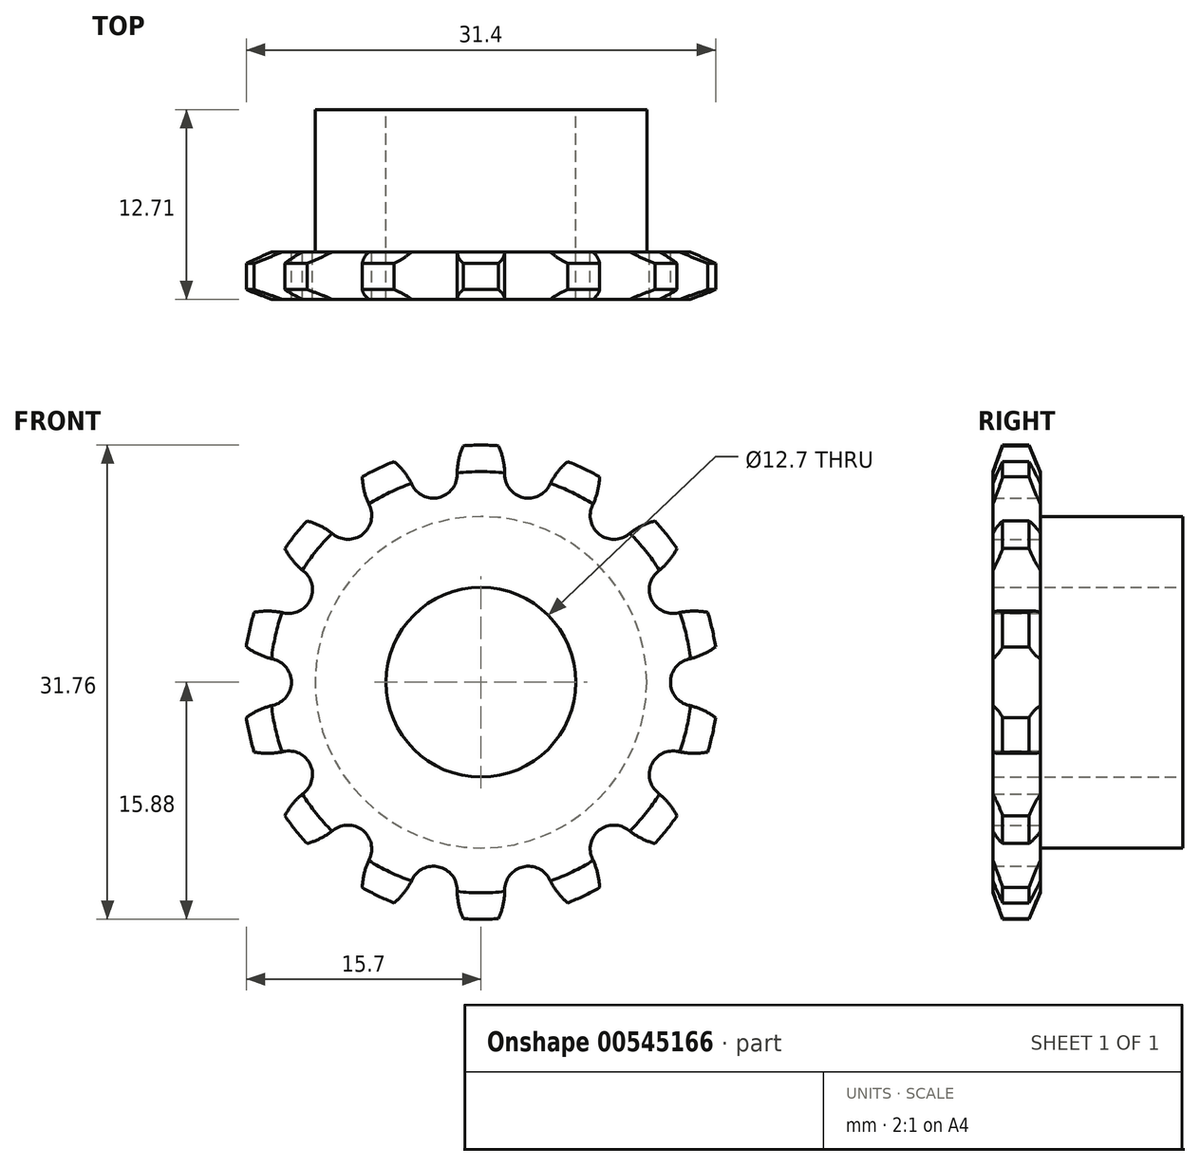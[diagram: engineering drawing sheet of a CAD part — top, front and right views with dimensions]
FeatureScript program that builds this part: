
annotation { "Feature Type Name" : "Feature", "Feature Type Description" : "" }
export const myFeature = defineFeature(function(context is Context, id is Id, definition is map)
    precondition{}
    {
        {
            var Q0;
            Q0=qCreatedBy(makeId("Front.planeOp"),FACE);
            var sketch = newSketch(context, id + "F0", { "sketchPlane" : qUnion([Q0])});
            skCircle(sketch, "E0.cCircle", {"center": v(0, 0) * mm, "radius": 13.91 * mm, "construction": true});
            skLineSegment(sketch, "E0.0", {"start": v(-3.17, 13.91) * mm, "end": v(3.17, 13.91) * mm, "construction": true});
            skLineSegment(sketch, "E0.1", {"start": v(3.18, 13.91) * mm, "end": v(8.9, 11.16) * mm, "construction": true});
            skLineSegment(sketch, "E0.2", {"start": v(8.9, 11.16) * mm, "end": v(12.86, 6.2) * mm, "construction": true});
            skLineSegment(sketch, "E0.3", {"start": v(12.86, 6.2) * mm, "end": v(14.27, 0) * mm, "construction": true});
            skLineSegment(sketch, "E0.4", {"start": v(14.27, 0) * mm, "end": v(12.86, -6.2) * mm, "construction": true});
            skLineSegment(sketch, "E0.5", {"start": v(12.86, -6.2) * mm, "end": v(8.9, -11.16) * mm, "construction": true});
            skLineSegment(sketch, "E0.6", {"start": v(8.9, -11.16) * mm, "end": v(3.18, -13.91) * mm, "construction": true});
            skLineSegment(sketch, "E0.7", {"start": v(3.17, -13.91) * mm, "end": v(-3.17, -13.91) * mm, "construction": true});
            skLineSegment(sketch, "E0.8", {"start": v(-3.17, -13.91) * mm, "end": v(-8.9, -11.16) * mm, "construction": true});
            skLineSegment(sketch, "E0.9", {"start": v(-8.9, -11.16) * mm, "end": v(-12.86, -6.2) * mm, "construction": true});
            skLineSegment(sketch, "E0.10", {"start": v(-12.86, -6.2) * mm, "end": v(-14.27, 0) * mm, "construction": true});
            skLineSegment(sketch, "E0.11", {"start": v(-14.27, 0) * mm, "end": v(-12.86, 6.2) * mm, "construction": true});
            skLineSegment(sketch, "E0.12", {"start": v(-12.86, 6.2) * mm, "end": v(-8.9, 11.16) * mm, "construction": true});
            skLineSegment(sketch, "E0.13", {"start": v(-8.9, 11.16) * mm, "end": v(-3.18, 13.91) * mm, "construction": true});
            skPoint(sketch, "E0.0.midPoint", {"position": v(0, 13.91) * mm});
            skCircle(sketch, "E1", {"center": v(3.17, 13.91) * mm, "radius": 1.59 * mm});
            skCircle(sketch, "E2", {"center": v(-3.17, 13.91) * mm, "radius": 1.59 * mm});
            skCircle(sketch, "E3", {"center": v(8.9, 11.16) * mm, "radius": 1.59 * mm});
            skCircle(sketch, "E4", {"center": v(-8.9, 11.16) * mm, "radius": 1.59 * mm});
            skCircle(sketch, "E5", {"center": v(-12.86, 6.2) * mm, "radius": 1.59 * mm});
            skCircle(sketch, "E6", {"center": v(-14.27, 0) * mm, "radius": 1.59 * mm});
            skCircle(sketch, "E7", {"center": v(12.86, 6.2) * mm, "radius": 1.59 * mm});
            skCircle(sketch, "E8", {"center": v(14.27, 0) * mm, "radius": 1.59 * mm});
            skCircle(sketch, "E9", {"center": v(12.86, -6.2) * mm, "radius": 1.59 * mm});
            skCircle(sketch, "E10", {"center": v(8.9, -11.16) * mm, "radius": 1.59 * mm});
            skCircle(sketch, "E11", {"center": v(3.18, -13.91) * mm, "radius": 1.59 * mm});
            skCircle(sketch, "E12", {"center": v(-12.86, -6.2) * mm, "radius": 1.59 * mm});
            skCircle(sketch, "E13", {"center": v(-8.9, -11.16) * mm, "radius": 1.59 * mm});
            skCircle(sketch, "E14", {"center": v(-3.17, -13.91) * mm, "radius": 1.59 * mm});
            skCircle(sketch, "E15", {"center": v(0, 0) * mm, "radius": 15.88 * mm});
            skArc(sketch, "E16", {"start": v(-1.59, 13.91) * mm, "mid": v(-1.17, 15.85) * mm, "end": v(0, 17.46) * mm});
            skArc(sketch, "E17", {"start": v(1.59, 13.91) * mm, "mid": v(1.17, 15.85) * mm, "end": v(0, 17.46) * mm});
            skArc(sketch, "E18", {"start": v(7.47, 11.84) * mm, "mid": v(7.94, 13.78) * mm, "end": v(7.58, 15.73) * mm});
            skArc(sketch, "E19", {"start": v(4.6, 13.22) * mm, "mid": v(5.82, 14.8) * mm, "end": v(7.58, 15.73) * mm});
            skArc(sketch, "E20", {"start": v(11.87, 7.43) * mm, "mid": v(13.13, 8.97) * mm, "end": v(13.65, 10.89) * mm});
            skArc(sketch, "E21", {"start": v(9.89, 9.91) * mm, "mid": v(11.66, 10.8) * mm, "end": v(13.65, 10.89) * mm});
            skArc(sketch, "E22", {"start": v(13.2, 4.64) * mm, "mid": v(15.2, 4.67) * mm, "end": v(17.02, 3.89) * mm});
            skArc(sketch, "E23", {"start": v(13.92, 1.55) * mm, "mid": v(15.72, 2.38) * mm, "end": v(17.02, 3.89) * mm});
            skArc(sketch, "E24", {"start": v(13.2, -4.64) * mm, "mid": v(15.2, -4.67) * mm, "end": v(17.02, -3.89) * mm});
            skArc(sketch, "E25", {"start": v(13.92, -1.55) * mm, "mid": v(15.72, -2.38) * mm, "end": v(17.02, -3.89) * mm});
            skArc(sketch, "E26", {"start": v(9.89, -9.91) * mm, "mid": v(11.66, -10.8) * mm, "end": v(13.65, -10.89) * mm});
            skArc(sketch, "E27", {"start": v(11.87, -7.43) * mm, "mid": v(13.13, -8.97) * mm, "end": v(13.65, -10.89) * mm});
            skArc(sketch, "E28", {"start": v(7.47, -11.84) * mm, "mid": v(7.94, -13.78) * mm, "end": v(7.58, -15.73) * mm});
            skArc(sketch, "E29", {"start": v(4.6, -13.22) * mm, "mid": v(5.82, -14.8) * mm, "end": v(7.58, -15.73) * mm});
            skArc(sketch, "E30", {"start": v(1.59, -13.91) * mm, "mid": v(1.17, -15.85) * mm, "end": v(0, -17.46) * mm});
            skArc(sketch, "E31", {"start": v(-1.59, -13.91) * mm, "mid": v(-1.17, -15.85) * mm, "end": v(0, -17.46) * mm});
            skArc(sketch, "E32", {"start": v(-4.6, -13.22) * mm, "mid": v(-5.82, -14.8) * mm, "end": v(-7.58, -15.73) * mm});
            skArc(sketch, "E33", {"start": v(-7.47, -11.84) * mm, "mid": v(-7.94, -13.78) * mm, "end": v(-7.58, -15.73) * mm});
            skArc(sketch, "E34", {"start": v(-11.8, -7.37) * mm, "mid": v(-13.1, -8.93) * mm, "end": v(-13.65, -10.89) * mm});
            skArc(sketch, "E35", {"start": v(-9.89, -9.91) * mm, "mid": v(-11.67, -10.8) * mm, "end": v(-13.65, -10.89) * mm});
            skArc(sketch, "E36", {"start": v(-13.92, -1.55) * mm, "mid": v(-15.72, -2.38) * mm, "end": v(-17.02, -3.89) * mm});
            skArc(sketch, "E37", {"start": v(-13.2, -4.64) * mm, "mid": v(-15.2, -4.67) * mm, "end": v(-17.02, -3.89) * mm});
            skArc(sketch, "E38", {"start": v(-13.92, 1.55) * mm, "mid": v(-15.72, 2.38) * mm, "end": v(-17.02, 3.89) * mm});
            skArc(sketch, "E39", {"start": v(-13.2, 4.64) * mm, "mid": v(-15.2, 4.67) * mm, "end": v(-17.02, 3.89) * mm});
            skArc(sketch, "E40", {"start": v(-9.89, 9.91) * mm, "mid": v(-11.66, 10.8) * mm, "end": v(-13.65, 10.89) * mm});
            skArc(sketch, "E41", {"start": v(-11.87, 7.43) * mm, "mid": v(-13.13, 8.97) * mm, "end": v(-13.65, 10.89) * mm});
            skArc(sketch, "E42", {"start": v(-4.6, 13.22) * mm, "mid": v(-5.82, 14.8) * mm, "end": v(-7.58, 15.73) * mm});
            skArc(sketch, "E43", {"start": v(-7.47, 11.84) * mm, "mid": v(-7.94, 13.78) * mm, "end": v(-7.58, 15.73) * mm});
            skCircle(sketch, "E44", {"center": v(0, 0) * mm, "radius": 6.35 * mm});
            skCircle(sketch, "E45", {"center": v(0, 0) * mm, "radius": 11.1 * mm});
            skSolve(sketch);
        }
        {
            var Q0;
            Q0=makeQuery(id+"F0.imprint","IMPRINT",FACE,{"disambiguationData":[TD([[makeQuery(id+"F0.imprint","IMPRINT",EDGE,{"derivedFrom":sQuery(id+"F0.wireOp",EDGE,"E45")}),-1.0]])]});
            var Q1;
            Q1=makeQuery(id+"F0.imprint","IMPRINT",FACE,{"disambiguationData":[TD([[makeQuery(id+"F0.imprint","IMPRINT",EDGE,{"derivedFrom":sQuery(id+"F0.wireOp",EDGE,"E44")}),-1.0]])]});
            extrude(context, id + "F1", {"entities" : qUnion([Q0, Q1]), "depth" : 3.17 * mm, "offsetDistance" : 25.4 * mm});
        }
        {
            var Q0;
            Q0=makeQuery(id+"F0.imprint","IMPRINT",FACE,{"disambiguationData":[TD([[makeQuery(id+"F0.imprint","IMPRINT",EDGE,{"derivedFrom":sQuery(id+"F0.wireOp",EDGE,"E44")}),-1.0]])]});
            extrude(context, id + "F2", {"entities" : qUnion([Q0]), "operationType" : NewBodyOperationType.ADD, "oppositeDirection" : true, "depth" : 9.52 * mm, "offsetDistance" : 25.4 * mm});
        }
        {
            var Q0;
            {var subQ0=sQuery(id+"F0.wireOp",EDGE,"E15");Q0=makeQuery(id+"F1.opExtrude","CAP_EDGE",EDGE,{"disambiguationData":[OSD([subQ0]),TDD([makeQuery(id+"F0.imprint","IMPRINT",EDGE,{"disambiguationData":[TD([[makeQuery(id+"F0.imprint","INTERSECT",VERTEX,{"derivedFrom":[subQ0,sQuery(id+"F0.wireOp",EDGE,"E22")]}),1.0]])],"derivedFrom":subQ0})])],"isStart":true});}
            var Q1;
            {var subQ0=sQuery(id+"F0.wireOp",EDGE,"E15");Q1=makeQuery(id+"F1.opExtrude","CAP_EDGE",EDGE,{"disambiguationData":[OSD([subQ0]),TDD([makeQuery(id+"F0.imprint","IMPRINT",EDGE,{"disambiguationData":[TD([[makeQuery(id+"F0.imprint","INTERSECT",VERTEX,{"derivedFrom":[subQ0,sQuery(id+"F0.wireOp",EDGE,"E24")]}),-1.0]])],"derivedFrom":subQ0})])],"isStart":true});}
            var Q2;
            {var subQ0=sQuery(id+"F0.wireOp",EDGE,"E15");Q2=makeQuery(id+"F1.opExtrude","CAP_EDGE",EDGE,{"disambiguationData":[OSD([subQ0]),TDD([makeQuery(id+"F0.imprint","IMPRINT",EDGE,{"disambiguationData":[TD([[makeQuery(id+"F0.imprint","INTERSECT",VERTEX,{"derivedFrom":[subQ0,sQuery(id+"F0.wireOp",EDGE,"E26")]}),-1.0]])],"derivedFrom":subQ0})])],"isStart":true});}
            var Q3;
            {var subQ0=sQuery(id+"F0.wireOp",EDGE,"E15");Q3=makeQuery(id+"F1.opExtrude","CAP_EDGE",EDGE,{"disambiguationData":[OSD([subQ0]),TDD([makeQuery(id+"F0.imprint","IMPRINT",EDGE,{"disambiguationData":[TD([[makeQuery(id+"F0.imprint","INTERSECT",VERTEX,{"derivedFrom":[subQ0,sQuery(id+"F0.wireOp",EDGE,"E29")]}),-1.0]])],"derivedFrom":subQ0})])],"isStart":true});}
            var Q4;
            {var subQ0=sQuery(id+"F0.wireOp",EDGE,"E15");Q4=makeQuery(id+"F1.opExtrude","CAP_EDGE",EDGE,{"disambiguationData":[OSD([subQ0]),TDD([makeQuery(id+"F0.imprint","IMPRINT",EDGE,{"disambiguationData":[TD([[makeQuery(id+"F0.imprint","INTERSECT",VERTEX,{"derivedFrom":[subQ0,sQuery(id+"F0.wireOp",EDGE,"E31")]}),-1.0]])],"derivedFrom":subQ0})])],"isStart":true});}
            var Q5;
            {var subQ0=sQuery(id+"F0.wireOp",EDGE,"E15");Q5=makeQuery(id+"F1.opExtrude","CAP_EDGE",EDGE,{"disambiguationData":[OSD([subQ0]),TDD([makeQuery(id+"F0.imprint","IMPRINT",EDGE,{"disambiguationData":[TD([[makeQuery(id+"F0.imprint","INTERSECT",VERTEX,{"derivedFrom":[subQ0,sQuery(id+"F0.wireOp",EDGE,"E33")]}),-1.0]])],"derivedFrom":subQ0})])],"isStart":true});}
            var Q6;
            {var subQ0=sQuery(id+"F0.wireOp",EDGE,"E15");Q6=makeQuery(id+"F1.opExtrude","CAP_EDGE",EDGE,{"disambiguationData":[OSD([subQ0]),TDD([makeQuery(id+"F0.imprint","IMPRINT",EDGE,{"disambiguationData":[TD([[makeQuery(id+"F0.imprint","INTERSECT",VERTEX,{"derivedFrom":[subQ0,sQuery(id+"F0.wireOp",EDGE,"E34")]}),-1.0]])],"derivedFrom":subQ0})])],"isStart":true});}
            var Q7;
            {var subQ0=sQuery(id+"F0.wireOp",EDGE,"E15");Q7=makeQuery(id+"F1.opExtrude","CAP_EDGE",EDGE,{"disambiguationData":[OSD([subQ0]),TDD([makeQuery(id+"F0.imprint","IMPRINT",EDGE,{"disambiguationData":[TD([[makeQuery(id+"F0.imprint","INTERSECT",VERTEX,{"derivedFrom":[subQ0,sQuery(id+"F0.wireOp",EDGE,"E36")]}),-1.0]])],"derivedFrom":subQ0})])],"isStart":true});}
            var Q8;
            {var subQ0=sQuery(id+"F0.wireOp",EDGE,"E15");Q8=makeQuery(id+"F1.opExtrude","CAP_EDGE",EDGE,{"disambiguationData":[OSD([subQ0]),TDD([makeQuery(id+"F0.imprint","IMPRINT",EDGE,{"disambiguationData":[TD([[makeQuery(id+"F0.imprint","INTERSECT",VERTEX,{"derivedFrom":[subQ0,sQuery(id+"F0.wireOp",EDGE,"E39")]}),-1.0]])],"derivedFrom":subQ0})])],"isStart":true});}
            var Q9;
            {var subQ0=sQuery(id+"F0.wireOp",EDGE,"E15");Q9=makeQuery(id+"F1.opExtrude","CAP_EDGE",EDGE,{"disambiguationData":[OSD([subQ0]),TDD([makeQuery(id+"F0.imprint","IMPRINT",EDGE,{"disambiguationData":[TD([[makeQuery(id+"F0.imprint","INTERSECT",VERTEX,{"derivedFrom":[subQ0,sQuery(id+"F0.wireOp",EDGE,"E40")]}),-1.0]])],"derivedFrom":subQ0})])],"isStart":true});}
            var Q10;
            {var subQ0=sQuery(id+"F0.wireOp",EDGE,"E15");Q10=makeQuery(id+"F1.opExtrude","CAP_EDGE",EDGE,{"disambiguationData":[OSD([subQ0]),TDD([makeQuery(id+"F0.imprint","IMPRINT",EDGE,{"disambiguationData":[TD([[makeQuery(id+"F0.imprint","INTERSECT",VERTEX,{"derivedFrom":[subQ0,sQuery(id+"F0.wireOp",EDGE,"E42")]}),-1.0]])],"derivedFrom":subQ0})])],"isStart":true});}
            var Q11;
            {var subQ0=sQuery(id+"F0.wireOp",EDGE,"E15");Q11=makeQuery(id+"F1.opExtrude","CAP_EDGE",EDGE,{"disambiguationData":[OSD([subQ0]),TDD([makeQuery(id+"F0.imprint","IMPRINT",EDGE,{"disambiguationData":[TD([[makeQuery(id+"F0.imprint","INTERSECT",VERTEX,{"derivedFrom":[subQ0,sQuery(id+"F0.wireOp",EDGE,"E17")]}),-1.0]])],"derivedFrom":subQ0})])],"isStart":true});}
            var Q12;
            {var subQ0=sQuery(id+"F0.wireOp",EDGE,"E15");Q12=makeQuery(id+"F1.opExtrude","CAP_EDGE",EDGE,{"disambiguationData":[OSD([subQ0]),TDD([makeQuery(id+"F0.imprint","IMPRINT",EDGE,{"disambiguationData":[TD([[makeQuery(id+"F0.imprint","INTERSECT",VERTEX,{"derivedFrom":[subQ0,sQuery(id+"F0.wireOp",EDGE,"E18")]}),-1.0]])],"derivedFrom":subQ0})])],"isStart":true});}
            var Q13;
            {var subQ0=sQuery(id+"F0.wireOp",EDGE,"E15");Q13=makeQuery(id+"F1.opExtrude","CAP_EDGE",EDGE,{"disambiguationData":[OSD([subQ0]),TDD([makeQuery(id+"F0.imprint","IMPRINT",EDGE,{"disambiguationData":[TD([[makeQuery(id+"F0.imprint","INTERSECT",VERTEX,{"derivedFrom":[subQ0,sQuery(id+"F0.wireOp",EDGE,"E20")]}),-1.0]])],"derivedFrom":subQ0})])],"isStart":true});}
            chamfer(context, id + "F3", {"entities" : qUnion([Q0, Q1, Q2, Q3, Q4, Q5, Q6, Q7, Q8, Q9, Q10, Q11, Q12, Q13]), "chamferType" : ChamferType.OFFSET_ANGLE, "width" : 0.76 * mm, "oppositeDirection" : false, "angle" : 67 * degree, "tangentPropagation" : true});
        }
        {
            var Q0;
            {var subQ0=sQuery(id+"F0.wireOp",EDGE,"E15");Q0=makeQuery(id+"F1.opExtrude","CAP_EDGE",EDGE,{"disambiguationData":[OSD([subQ0]),TDD([makeQuery(id+"F0.imprint","IMPRINT",EDGE,{"disambiguationData":[TD([[makeQuery(id+"F0.imprint","INTERSECT",VERTEX,{"derivedFrom":[subQ0,sQuery(id+"F0.wireOp",EDGE,"E17")]}),-1.0]])],"derivedFrom":subQ0})])],"isStart":false});}
            var Q1;
            {var subQ0=sQuery(id+"F0.wireOp",EDGE,"E15");Q1=makeQuery(id+"F1.opExtrude","CAP_EDGE",EDGE,{"disambiguationData":[OSD([subQ0]),TDD([makeQuery(id+"F0.imprint","IMPRINT",EDGE,{"disambiguationData":[TD([[makeQuery(id+"F0.imprint","INTERSECT",VERTEX,{"derivedFrom":[subQ0,sQuery(id+"F0.wireOp",EDGE,"E18")]}),-1.0]])],"derivedFrom":subQ0})])],"isStart":false});}
            var Q2;
            {var subQ0=sQuery(id+"F0.wireOp",EDGE,"E15");Q2=makeQuery(id+"F1.opExtrude","CAP_EDGE",EDGE,{"disambiguationData":[OSD([subQ0]),TDD([makeQuery(id+"F0.imprint","IMPRINT",EDGE,{"disambiguationData":[TD([[makeQuery(id+"F0.imprint","INTERSECT",VERTEX,{"derivedFrom":[subQ0,sQuery(id+"F0.wireOp",EDGE,"E20")]}),-1.0]])],"derivedFrom":subQ0})])],"isStart":false});}
            var Q3;
            {var subQ0=sQuery(id+"F0.wireOp",EDGE,"E15");Q3=makeQuery(id+"F1.opExtrude","CAP_EDGE",EDGE,{"disambiguationData":[OSD([subQ0]),TDD([makeQuery(id+"F0.imprint","IMPRINT",EDGE,{"disambiguationData":[TD([[makeQuery(id+"F0.imprint","INTERSECT",VERTEX,{"derivedFrom":[subQ0,sQuery(id+"F0.wireOp",EDGE,"E22")]}),1.0]])],"derivedFrom":subQ0})])],"isStart":false});}
            var Q4;
            {var subQ0=sQuery(id+"F0.wireOp",EDGE,"E15");Q4=makeQuery(id+"F1.opExtrude","CAP_EDGE",EDGE,{"disambiguationData":[OSD([subQ0]),TDD([makeQuery(id+"F0.imprint","IMPRINT",EDGE,{"disambiguationData":[TD([[makeQuery(id+"F0.imprint","INTERSECT",VERTEX,{"derivedFrom":[subQ0,sQuery(id+"F0.wireOp",EDGE,"E24")]}),-1.0]])],"derivedFrom":subQ0})])],"isStart":false});}
            var Q5;
            {var subQ0=sQuery(id+"F0.wireOp",EDGE,"E15");Q5=makeQuery(id+"F1.opExtrude","CAP_EDGE",EDGE,{"disambiguationData":[OSD([subQ0]),TDD([makeQuery(id+"F0.imprint","IMPRINT",EDGE,{"disambiguationData":[TD([[makeQuery(id+"F0.imprint","INTERSECT",VERTEX,{"derivedFrom":[subQ0,sQuery(id+"F0.wireOp",EDGE,"E26")]}),-1.0]])],"derivedFrom":subQ0})])],"isStart":false});}
            var Q6;
            {var subQ0=sQuery(id+"F0.wireOp",EDGE,"E15");Q6=makeQuery(id+"F1.opExtrude","CAP_EDGE",EDGE,{"disambiguationData":[OSD([subQ0]),TDD([makeQuery(id+"F0.imprint","IMPRINT",EDGE,{"disambiguationData":[TD([[makeQuery(id+"F0.imprint","INTERSECT",VERTEX,{"derivedFrom":[subQ0,sQuery(id+"F0.wireOp",EDGE,"E29")]}),-1.0]])],"derivedFrom":subQ0})])],"isStart":false});}
            var Q7;
            {var subQ0=sQuery(id+"F0.wireOp",EDGE,"E15");Q7=makeQuery(id+"F1.opExtrude","CAP_EDGE",EDGE,{"disambiguationData":[OSD([subQ0]),TDD([makeQuery(id+"F0.imprint","IMPRINT",EDGE,{"disambiguationData":[TD([[makeQuery(id+"F0.imprint","INTERSECT",VERTEX,{"derivedFrom":[subQ0,sQuery(id+"F0.wireOp",EDGE,"E31")]}),-1.0]])],"derivedFrom":subQ0})])],"isStart":false});}
            var Q8;
            {var subQ0=sQuery(id+"F0.wireOp",EDGE,"E15");Q8=makeQuery(id+"F1.opExtrude","CAP_EDGE",EDGE,{"disambiguationData":[OSD([subQ0]),TDD([makeQuery(id+"F0.imprint","IMPRINT",EDGE,{"disambiguationData":[TD([[makeQuery(id+"F0.imprint","INTERSECT",VERTEX,{"derivedFrom":[subQ0,sQuery(id+"F0.wireOp",EDGE,"E33")]}),-1.0]])],"derivedFrom":subQ0})])],"isStart":false});}
            var Q9;
            {var subQ0=sQuery(id+"F0.wireOp",EDGE,"E15");Q9=makeQuery(id+"F1.opExtrude","CAP_EDGE",EDGE,{"disambiguationData":[OSD([subQ0]),TDD([makeQuery(id+"F0.imprint","IMPRINT",EDGE,{"disambiguationData":[TD([[makeQuery(id+"F0.imprint","INTERSECT",VERTEX,{"derivedFrom":[subQ0,sQuery(id+"F0.wireOp",EDGE,"E34")]}),-1.0]])],"derivedFrom":subQ0})])],"isStart":false});}
            var Q10;
            {var subQ0=sQuery(id+"F0.wireOp",EDGE,"E15");Q10=makeQuery(id+"F1.opExtrude","CAP_EDGE",EDGE,{"disambiguationData":[OSD([subQ0]),TDD([makeQuery(id+"F0.imprint","IMPRINT",EDGE,{"disambiguationData":[TD([[makeQuery(id+"F0.imprint","INTERSECT",VERTEX,{"derivedFrom":[subQ0,sQuery(id+"F0.wireOp",EDGE,"E36")]}),-1.0]])],"derivedFrom":subQ0})])],"isStart":false});}
            var Q11;
            {var subQ0=sQuery(id+"F0.wireOp",EDGE,"E15");Q11=makeQuery(id+"F1.opExtrude","CAP_EDGE",EDGE,{"disambiguationData":[OSD([subQ0]),TDD([makeQuery(id+"F0.imprint","IMPRINT",EDGE,{"disambiguationData":[TD([[makeQuery(id+"F0.imprint","INTERSECT",VERTEX,{"derivedFrom":[subQ0,sQuery(id+"F0.wireOp",EDGE,"E39")]}),-1.0]])],"derivedFrom":subQ0})])],"isStart":false});}
            var Q12;
            {var subQ0=sQuery(id+"F0.wireOp",EDGE,"E15");Q12=makeQuery(id+"F1.opExtrude","CAP_EDGE",EDGE,{"disambiguationData":[OSD([subQ0]),TDD([makeQuery(id+"F0.imprint","IMPRINT",EDGE,{"disambiguationData":[TD([[makeQuery(id+"F0.imprint","INTERSECT",VERTEX,{"derivedFrom":[subQ0,sQuery(id+"F0.wireOp",EDGE,"E40")]}),-1.0]])],"derivedFrom":subQ0})])],"isStart":false});}
            var Q13;
            {var subQ0=sQuery(id+"F0.wireOp",EDGE,"E15");Q13=makeQuery(id+"F1.opExtrude","CAP_EDGE",EDGE,{"disambiguationData":[OSD([subQ0]),TDD([makeQuery(id+"F0.imprint","IMPRINT",EDGE,{"disambiguationData":[TD([[makeQuery(id+"F0.imprint","INTERSECT",VERTEX,{"derivedFrom":[subQ0,sQuery(id+"F0.wireOp",EDGE,"E42")]}),-1.0]])],"derivedFrom":subQ0})])],"isStart":false});}
            chamfer(context, id + "F4", {"entities" : qUnion([Q0, Q1, Q2, Q3, Q4, Q5, Q6, Q7, Q8, Q9, Q10, Q11, Q12, Q13]), "chamferType" : ChamferType.OFFSET_ANGLE, "width" : 1.78 * mm, "oppositeDirection" : false, "angle" : 20 * degree, "tangentPropagation" : true});
        }
    });
